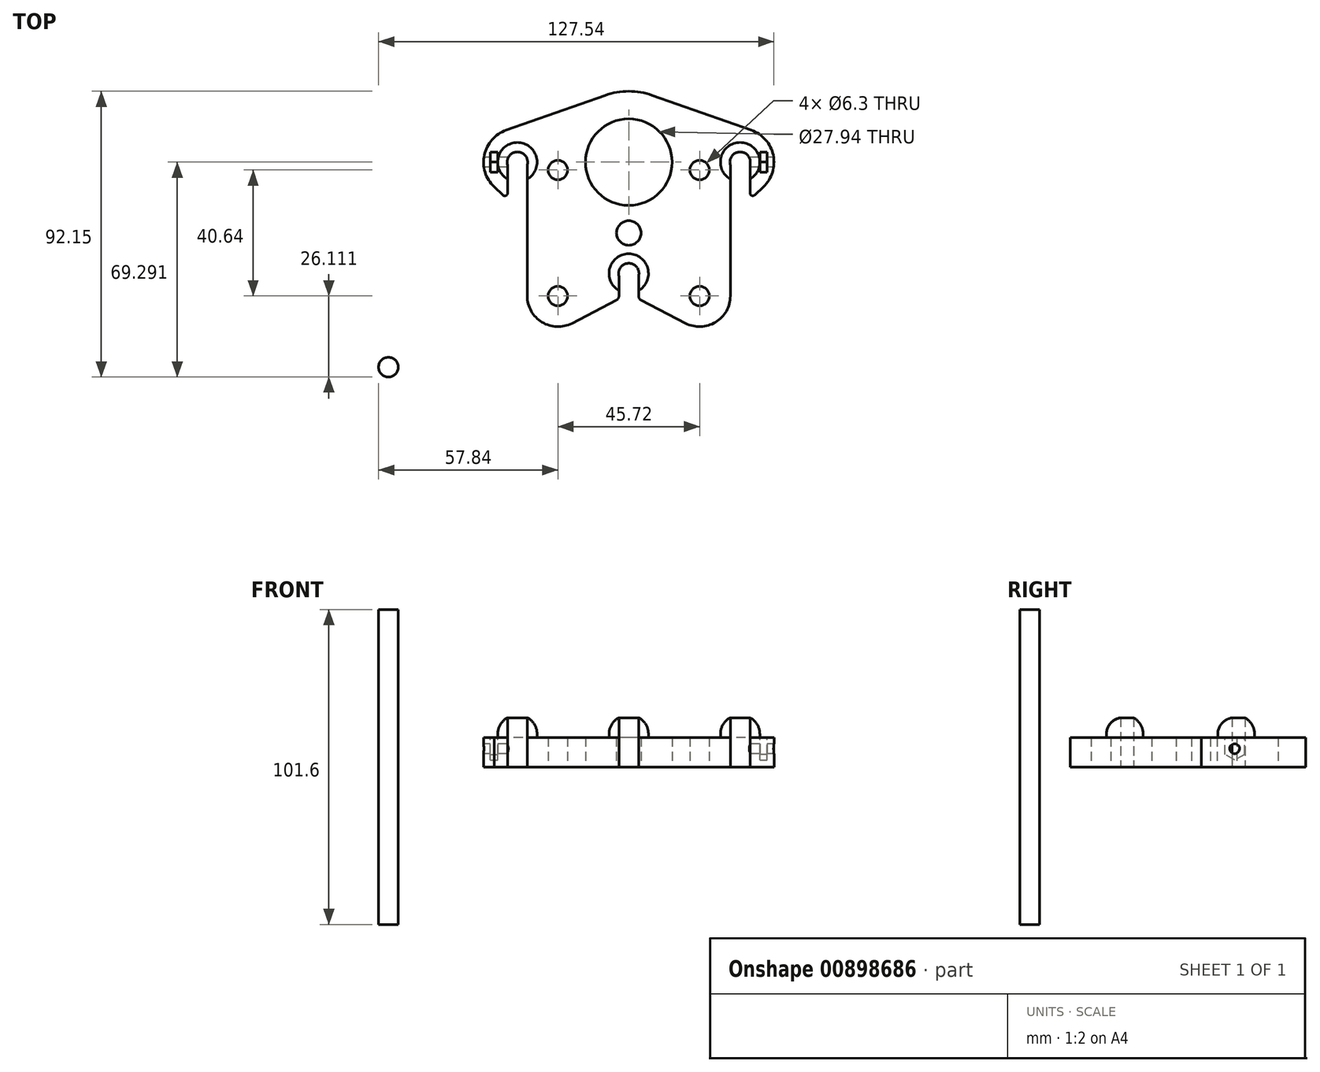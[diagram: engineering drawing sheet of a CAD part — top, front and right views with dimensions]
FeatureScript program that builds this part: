
annotation { "Feature Type Name" : "Feature", "Feature Type Description" : "" }
export const myFeature = defineFeature(function(context is Context, id is Id, definition is map)
    precondition{}
    {
        {
            var Q0;
            Q0=qCreatedBy(makeId("Top.planeOp"),FACE);
            var sketch = newSketch(context, id + "F0", { "sketchPlane" : qUnion([Q0])});
            skArc(sketch, "E0", {"start": v(3.18, -0.9) * mm, "mid": v(0, 3.3) * mm, "end": v(-3.18, -0.9) * mm});
            skArc(sketch, "E1", {"start": v(-32.75, 35.01) * mm, "mid": v(-35.92, 39.22) * mm, "end": v(-39.1, 35.01) * mm});
            skArc(sketch, "E2", {"start": v(39.1, 35.01) * mm, "mid": v(35.92, 39.22) * mm, "end": v(32.75, 35.01) * mm});
            skCircle(sketch, "E3", {"center": v(0, 35.92) * mm, "radius": 16.51 * mm});
            skArc(sketch, "E4.0", {"start": v(-39.55, 46.22) * mm, "mid": v(-46.6, 38.2) * mm, "end": v(-43.45, 28) * mm});
            skArc(sketch, "E5.0", {"start": v(7.6, 57.48) * mm, "mid": v(0, 58.78) * mm, "end": v(-7.6, 57.48) * mm});
            skArc(sketch, "E6.0", {"start": v(43.45, 28) * mm, "mid": v(46.6, 38.2) * mm, "end": v(39.55, 46.22) * mm});
            skLineSegment(sketch, "E7", {"start": v(-39.55, 46.22) * mm, "end": v(-7.6, 57.48) * mm});
            skLineSegment(sketch, "E8", {"start": v(7.6, 57.48) * mm, "end": v(39.55, 46.22) * mm});
            skLineSegment(sketch, "E9", {"start": v(43.45, 28) * mm, "end": v(40.64, 25.34) * mm});
            skCircle(sketch, "E10", {"center": v(-35.92, 35.92) * mm, "radius": 3.18 * mm, "construction": true});
            skCircle(sketch, "E11", {"center": v(35.92, 35.92) * mm, "radius": 3.18 * mm, "construction": true});
            skCircle(sketch, "E12", {"center": v(0, 0) * mm, "radius": 3.18 * mm, "construction": true});
            skLineSegment(sketch, "E13", {"start": v(-39.1, 35.92) * mm, "end": v(-39.1, 25.94) * mm});
            skLineSegment(sketch, "E14", {"start": v(-3.18, 0) * mm, "end": v(-3.17, -7.26) * mm});
            skLineSegment(sketch, "E15", {"start": v(3.17, 0) * mm, "end": v(3.18, -7.26) * mm});
            skPoint(sketch, "E16", {"position": v(-3.18, -0.9) * mm});
            skPoint(sketch, "E17", {"position": v(3.18, -0.9) * mm});
            skLineSegment(sketch, "E18.trimOffspring", {"start": v(-40.65, 25.28) * mm, "end": v(-43.45, 28) * mm});
            skPoint(sketch, "E19.visualSharp", {"position": v(-39.1, 23.76) * mm});
            skArc(sketch, "E19.filletArc", {"start": v(-40.65, 25.28) * mm, "mid": v(-39.66, 25.1) * mm, "end": v(-39.1, 25.94) * mm});
            skLineSegment(sketch, "E20", {"start": v(32.75, 35.92) * mm, "end": v(32.75, -7.26) * mm});
            skLineSegment(sketch, "E21", {"start": v(39.1, 35.92) * mm, "end": v(39.1, 26) * mm});
            skPoint(sketch, "E22.visualSharp", {"position": v(39.1, 23.87) * mm});
            skCircle(sketch, "E23.0", {"center": v(0, 35.92) * mm, "radius": 13.97 * mm});
            skLineSegment(sketch, "E24", {"start": v(0, 35.92) * mm, "end": v(0, 52.43) * mm, "construction": true});
            skArc(sketch, "E25.filletArc", {"start": v(39.1, 26) * mm, "mid": v(39.65, 25.16) * mm, "end": v(40.64, 25.34) * mm});
            skLineSegment(sketch, "E26", {"start": v(-35.92, 35.92) * mm, "end": v(35.92, 35.92) * mm, "construction": true});
            skCircle(sketch, "E27", {"center": v(-22.86, 33.38) * mm, "radius": 3.15 * mm});
            skCircle(sketch, "E28", {"center": v(22.86, 33.38) * mm, "radius": 3.15 * mm});
            skCircle(sketch, "E29", {"center": v(-22.86, -7.26) * mm, "radius": 3.15 * mm});
            skCircle(sketch, "E30", {"center": v(22.86, -7.26) * mm, "radius": 3.15 * mm});
            skLineSegment(sketch, "E31.bottom", {"start": v(-22.86, 33.38) * mm, "end": v(22.86, 33.38) * mm, "construction": true});
            skLineSegment(sketch, "E31.top", {"start": v(-22.86, -7.26) * mm, "end": v(22.86, -7.26) * mm, "construction": true});
            skLineSegment(sketch, "E31.left", {"start": v(-22.86, 33.38) * mm, "end": v(-22.86, -7.26) * mm, "construction": true});
            skLineSegment(sketch, "E31.right", {"start": v(22.86, 33.38) * mm, "end": v(22.86, -7.26) * mm, "construction": true});
            skLineSegment(sketch, "E32", {"start": v(0, 35.92) * mm, "end": v(0, -7.26) * mm, "construction": true});
            skArc(sketch, "E33.0", {"start": v(-32.75, -7.26) * mm, "mid": v(-28, -15.7) * mm, "end": v(-18.3, -16.03) * mm});
            skArc(sketch, "E34.0", {"start": v(18.3, -16.03) * mm, "mid": v(28, -15.7) * mm, "end": v(32.75, -7.26) * mm});
            skLineSegment(sketch, "E35", {"start": v(-4, -8.61) * mm, "end": v(-18.3, -16.03) * mm});
            skLineSegment(sketch, "E36", {"start": v(4, -8.61) * mm, "end": v(18.3, -16.03) * mm});
            skLineSegment(sketch, "E37", {"start": v(-32.75, 35.92) * mm, "end": v(-32.75, -7.26) * mm});
            skPoint(sketch, "E38.visualSharp", {"position": v(-3.17, -8.19) * mm});
            skArc(sketch, "E38.filletArc", {"start": v(-4, -8.61) * mm, "mid": v(-3.4, -8.05) * mm, "end": v(-3.18, -7.26) * mm});
            skPoint(sketch, "E39.visualSharp", {"position": v(3.17, -8.19) * mm});
            skArc(sketch, "E39.filletArc", {"start": v(3.17, -7.26) * mm, "mid": v(3.4, -8.05) * mm, "end": v(4, -8.61) * mm});
            skCircle(sketch, "E40", {"center": v(0, 13.06) * mm, "radius": 3.96 * mm});
            skSolve(sketch);
        }
        {
            var Q0;
            {var subQ5=sQuery(id+"F0.wireOp",EDGE,"E0");Q0=makeQuery(id+"F0.imprint","IMPRINT",FACE,{"disambiguationData":[TD([[makeQuery(id+"F0.imprint","IMPRINT",EDGE,{"derivedFrom":subQ5}),-1.0]])]});}
            extrude(context, id + "F1", {"entities" : qUnion([Q0]), "depth" : 9.52 * mm, "offsetDistance" : 25.4 * mm});
        }
        {
            var Q0;
            Q0=makeQuery(id+"F0.imprint","IMPRINT",FACE,{"disambiguationData":[TD([[makeQuery(id+"F0.imprint","IMPRINT",EDGE,{"derivedFrom":sQuery(id+"F0.wireOp",EDGE,"E3")}),1.0]])]});
            var Q1;
            Q1=makeQuery(id+"F1.opExtrude","CAP_FACE",FACE,{"disambiguationData":[OSD([sQuery(id+"F0.wireOp",EDGE,"E0"),sQuery(id+"F0.wireOp",EDGE,"E1"),sQuery(id+"F0.wireOp",EDGE,"E2"),sQuery(id+"F0.wireOp",EDGE,"E3"),sQuery(id+"F0.wireOp",EDGE,"E4.0"),sQuery(id+"F0.wireOp",EDGE,"E5.0"),sQuery(id+"F0.wireOp",EDGE,"E6.0"),sQuery(id+"F0.wireOp",EDGE,"E7"),sQuery(id+"F0.wireOp",EDGE,"E8"),sQuery(id+"F0.wireOp",EDGE,"E9"),sQuery(id+"F0.wireOp",EDGE,"E13"),sQuery(id+"F0.wireOp",EDGE,"E14"),sQuery(id+"F0.wireOp",EDGE,"E15"),sQuery(id+"F0.wireOp",EDGE,"E18.trimOffspring"),sQuery(id+"F0.wireOp",EDGE,"E19.filletArc"),sQuery(id+"F0.wireOp",EDGE,"E20"),sQuery(id+"F0.wireOp",EDGE,"E21"),sQuery(id+"F0.wireOp",EDGE,"E25.filletArc"),sQuery(id+"F0.wireOp",EDGE,"E27"),sQuery(id+"F0.wireOp",EDGE,"E28"),sQuery(id+"F0.wireOp",EDGE,"E29"),sQuery(id+"F0.wireOp",EDGE,"E30"),sQuery(id+"F0.wireOp",EDGE,"E33.0"),sQuery(id+"F0.wireOp",EDGE,"E34.0"),sQuery(id+"F0.wireOp",EDGE,"E35"),sQuery(id+"F0.wireOp",EDGE,"E36"),sQuery(id+"F0.wireOp",EDGE,"E37"),sQuery(id+"F0.wireOp",EDGE,"E38.filletArc"),sQuery(id+"F0.wireOp",EDGE,"E39.filletArc")])],"isStart":false});
            extrude(context, id + "F2", {"entities" : qUnion([Q0]), "operationType" : NewBodyOperationType.ADD, "endBound" : BoundingType.UP_TO_SURFACE, "depth" : 2.54 * mm, "endBoundEntityFace" : qUnion([Q1]), "offsetDistance" : 6.35 * mm});
        }
        {
            var Q0;
            Q0=makeQuery(id+"F1.opExtrude","CAP_FACE",FACE,{"disambiguationData":[OSD([sQuery(id+"F0.wireOp",EDGE,"E0"),sQuery(id+"F0.wireOp",EDGE,"E1"),sQuery(id+"F0.wireOp",EDGE,"E2"),sQuery(id+"F0.wireOp",EDGE,"E3"),sQuery(id+"F0.wireOp",EDGE,"E4.0"),sQuery(id+"F0.wireOp",EDGE,"E5.0"),sQuery(id+"F0.wireOp",EDGE,"E6.0"),sQuery(id+"F0.wireOp",EDGE,"02fbeba7-076e-4ed0-9f02-67362b93dccf.0"),sQuery(id+"F0.wireOp",EDGE,"E7"),sQuery(id+"F0.wireOp",EDGE,"E8"),sQuery(id+"F0.wireOp",EDGE,"E9"),sQuery(id+"F0.wireOp",EDGE,"bXI39tXD-kIKO-QA8d-uo1d-AjNWw4kzWSzn"),sQuery(id+"F0.wireOp",EDGE,"yvXXFvSa-JQHm-aZvy-wO3q-0ffgoC5Wr51Q"),sQuery(id+"F0.wireOp",EDGE,"E13"),sQuery(id+"F0.wireOp",EDGE,"E14"),sQuery(id+"F0.wireOp",EDGE,"E15"),sQuery(id+"F0.wireOp",EDGE,"1b80de2d-6fcf-4166-8bd7-bc7520118ab3.trimOffspring"),sQuery(id+"F0.wireOp",EDGE,"E18.trimOffspring"),sQuery(id+"F0.wireOp",EDGE,"E19.filletArc"),sQuery(id+"F0.wireOp",EDGE,"30e6a12d-ff62-4460-809b-2951cf116d4f.filletArc"),sQuery(id+"F0.wireOp",EDGE,"3d167f00-72a4-4ff5-8a6d-0d591a0e7773.filletArc"),sQuery(id+"F0.wireOp",EDGE,"E20"),sQuery(id+"F0.wireOp",EDGE,"E21"),sQuery(id+"F0.wireOp",EDGE,"02ed80ea-b338-46f1-988c-5186e078d909.trimOffspring"),sQuery(id+"F0.wireOp",EDGE,"3LgmcLzA-5pnU-fFz7-q1u9-bpeBtAsCO3An"),sQuery(id+"F0.wireOp",EDGE,"4eo9xTR6-c1Fu-en91-zOid-S4E7wj55DmDX"),sQuery(id+"F0.wireOp",EDGE,"E25.filletArc"),sQuery(id+"F0.wireOp",EDGE,"0de4be46-af92-408f-a28e-b5eb566cc358.filletArc"),sQuery(id+"F0.wireOp",EDGE,"cd97e584-8722-4711-bad1-4d169eb79cda.filletArc"),sQuery(id+"F0.wireOp",EDGE,"a80f9f6f-3806-41d0-9fd0-596e0330244b.filletArc"),sQuery(id+"F0.wireOp",EDGE,"743a1c7c-530f-41f0-bede-06812bb20fe3.filletArc")])],"isStart":false});
            var sketch = newSketch(context, id + "F3", { "sketchPlane" : qUnion([Q0])});
            skCircle(sketch, "E41", {"center": v(-35.92, 35.92) * mm, "radius": 6.35 * mm});
            skCircle(sketch, "E42", {"center": v(35.92, 35.92) * mm, "radius": 6.35 * mm});
            skCircle(sketch, "E43", {"center": v(0, 0) * mm, "radius": 6.35 * mm});
            skSolve(sketch);
        }
        {
            var Q0;
            Q0=makeQuery(id+"F1.opExtrude","CAP_FACE",FACE,{"disambiguationData":[OSD([sQuery(id+"F0.wireOp",EDGE,"E0"),sQuery(id+"F0.wireOp",EDGE,"E1"),sQuery(id+"F0.wireOp",EDGE,"E2"),sQuery(id+"F0.wireOp",EDGE,"E3"),sQuery(id+"F0.wireOp",EDGE,"E4.0"),sQuery(id+"F0.wireOp",EDGE,"E5.0"),sQuery(id+"F0.wireOp",EDGE,"E6.0"),sQuery(id+"F0.wireOp",EDGE,"02fbeba7-076e-4ed0-9f02-67362b93dccf.0"),sQuery(id+"F0.wireOp",EDGE,"E7"),sQuery(id+"F0.wireOp",EDGE,"E8"),sQuery(id+"F0.wireOp",EDGE,"E9"),sQuery(id+"F0.wireOp",EDGE,"bXI39tXD-kIKO-QA8d-uo1d-AjNWw4kzWSzn"),sQuery(id+"F0.wireOp",EDGE,"yvXXFvSa-JQHm-aZvy-wO3q-0ffgoC5Wr51Q"),sQuery(id+"F0.wireOp",EDGE,"E13"),sQuery(id+"F0.wireOp",EDGE,"E14"),sQuery(id+"F0.wireOp",EDGE,"E15"),sQuery(id+"F0.wireOp",EDGE,"1b80de2d-6fcf-4166-8bd7-bc7520118ab3.trimOffspring"),sQuery(id+"F0.wireOp",EDGE,"E18.trimOffspring"),sQuery(id+"F0.wireOp",EDGE,"E19.filletArc"),sQuery(id+"F0.wireOp",EDGE,"2f08ad09-a47d-42bd-8f0e-b7f58f6490e4.filletArc"),sQuery(id+"F0.wireOp",EDGE,"30e6a12d-ff62-4460-809b-2951cf116d4f.filletArc"),sQuery(id+"F0.wireOp",EDGE,"3d167f00-72a4-4ff5-8a6d-0d591a0e7773.filletArc"),sQuery(id+"F0.wireOp",EDGE,"E20"),sQuery(id+"F0.wireOp",EDGE,"E21"),sQuery(id+"F0.wireOp",EDGE,"02ed80ea-b338-46f1-988c-5186e078d909.trimOffspring"),sQuery(id+"F0.wireOp",EDGE,"bfc3d6b4-ed7b-404a-8939-94d15189dd00.filletArc"),sQuery(id+"F0.wireOp",EDGE,"E22.filletArc")])],"isStart":false});
            var sketch = newSketch(context, id + "F4", { "sketchPlane" : qUnion([Q0])});
            skPoint(sketch, "E44.center", {"position": v(0, 35.92) * mm});
            skCircle(sketch, "E45", {"center": v(-35.92, 35.92) * mm, "radius": 6.35 * mm});
            skCircle(sketch, "E46", {"center": v(35.92, 35.92) * mm, "radius": 6.35 * mm});
            skCircle(sketch, "E47", {"center": v(0, 0) * mm, "radius": 6.35 * mm});
            skLineSegment(sketch, "E48", {"start": v(-42.27, 39.15) * mm, "end": v(-42.27, 32.7) * mm});
            skLineSegment(sketch, "E49", {"start": v(-42.27, 32.7) * mm, "end": v(-44.6, 32.7) * mm});
            skLineSegment(sketch, "E50", {"start": v(-44.6, 32.7) * mm, "end": v(-44.6, 39.15) * mm});
            skLineSegment(sketch, "E51", {"start": v(-44.6, 39.15) * mm, "end": v(-42.27, 39.15) * mm});
            skLineSegment(sketch, "E52", {"start": v(-35.92, 35.92) * mm, "end": v(-42.27, 35.92) * mm, "construction": true});
            skLineSegment(sketch, "E53", {"start": v(42.27, 32.7) * mm, "end": v(42.27, 39.15) * mm});
            skLineSegment(sketch, "E54", {"start": v(42.27, 39.15) * mm, "end": v(44.6, 39.15) * mm});
            skLineSegment(sketch, "E55", {"start": v(44.6, 39.15) * mm, "end": v(44.6, 32.7) * mm});
            skLineSegment(sketch, "E56", {"start": v(44.6, 32.7) * mm, "end": v(42.27, 32.7) * mm});
            skLineSegment(sketch, "E57", {"start": v(35.92, 35.92) * mm, "end": v(42.27, 35.92) * mm, "construction": true});
            skSolve(sketch);
        }
        {
            var Q0;
            Q0=makeQuery(id+"F4.imprint","IMPRINT",FACE,{"disambiguationData":[TD([[makeQuery(id+"F4.imprint","IMPRINT",EDGE,{"derivedFrom":sQuery(id+"F4.wireOp",EDGE,"E44.2.0")}),-1.0]])]});
            var Q1;
            {var subQ3=sQuery(id+"F4.wireOp",EDGE,"d1FFw4VD-CotE-ErUC-aBlM-ySrozfUtPZIG");Q1=makeQuery(id+"F4.imprint","IMPRINT",FACE,{"disambiguationData":[TD([[makeQuery(id+"F4.imprint","IMPRINT",EDGE,{"derivedFrom":subQ3}),-1.0]])]});}
            var Q2;
            Q2=makeQuery(id+"F4.imprint","IMPRINT",FACE,{"disambiguationData":[TD([[makeQuery(id+"F4.imprint","IMPRINT",EDGE,{"derivedFrom":sQuery(id+"F4.wireOp",EDGE,"E44.1.0")}),-1.0]])]});
            var Q3;
            {var subQ0=sQuery(id+"F4.wireOp",EDGE,"E49");Q3=makeQuery(id+"F4.imprint","IMPRINT",FACE,{"disambiguationData":[TD([[makeQuery(id+"F4.imprint","IMPRINT",EDGE,{"derivedFrom":subQ0}),-1.0]])]});}
            var Q4;
            {var subQ0=sQuery(id+"F4.wireOp",EDGE,"E54");Q4=makeQuery(id+"F4.imprint","IMPRINT",FACE,{"disambiguationData":[TD([[makeQuery(id+"F4.imprint","IMPRINT",EDGE,{"derivedFrom":subQ0}),-1.0]])]});}
            var Q5;
            Q5=makeQuery(id+"F4.imprint","IMPRINT",FACE,{"disambiguationData":[TD([[makeQuery(id+"F4.imprint","IMPRINT",EDGE,{"derivedFrom":sQuery(id+"F4.wireOp",EDGE,"1bb13d12-811f-4404-9e1d-75ced0edb1cc")}),-1.0]])]});
            extrude(context, id + "F5", {"entities" : qUnion([Q0, Q1, Q2, Q3, Q4, Q5]), "operationType" : NewBodyOperationType.REMOVE, "oppositeDirection" : true, "depth" : 8.64 * mm, "offsetDistance" : 25.4 * mm});
        }
        {
            var Q0;
            Q0=makeQuery(id+"F5.boolean.opBoolean","COPY",EDGE,{"derivedFrom":makeQuery(id+"F5.opExtrude","CAP_EDGE",EDGE,{"disambiguationData":[OSD([sQuery(id+"F4.wireOp",EDGE,"E44.1.1")])],"isStart":false})});
            var Q1;
            Q1=makeQuery(id+"F5.boolean.opBoolean","COPY",EDGE,{"derivedFrom":makeQuery(id+"F5.opExtrude","CAP_EDGE",EDGE,{"disambiguationData":[OSD([sQuery(id+"F4.wireOp",EDGE,"E44.1.3")])],"isStart":false})});
            var Q2;
            Q2=makeQuery(id+"F5.boolean.opBoolean","COPY",EDGE,{"derivedFrom":makeQuery(id+"F5.opExtrude","CAP_EDGE",EDGE,{"disambiguationData":[OSD([sQuery(id+"F4.wireOp",EDGE,"d1FFw4VD-CotE-ErUC-aBlM-ySrozfUtPZIG")])],"isStart":false})});
            var Q3;
            Q3=makeQuery(id+"F5.boolean.opBoolean","COPY",EDGE,{"derivedFrom":makeQuery(id+"F5.opExtrude","CAP_EDGE",EDGE,{"disambiguationData":[OSD([sQuery(id+"F4.wireOp",EDGE,"UtWCcdUI-wfrM-d3JI-pGr6-eE53RfRw4Zsa")])],"isStart":false})});
            var Q4;
            Q4=makeQuery(id+"F5.boolean.opBoolean","COPY",EDGE,{"derivedFrom":makeQuery(id+"F5.opExtrude","CAP_EDGE",EDGE,{"disambiguationData":[OSD([sQuery(id+"F4.wireOp",EDGE,"E44.2.3")])],"isStart":false})});
            var Q5;
            Q5=makeQuery(id+"F5.boolean.opBoolean","COPY",EDGE,{"derivedFrom":makeQuery(id+"F5.opExtrude","CAP_EDGE",EDGE,{"disambiguationData":[OSD([sQuery(id+"F4.wireOp",EDGE,"E44.2.1")])],"isStart":false})});
            var Q6;
            Q6=makeQuery(id+"F5.boolean.opBoolean","COPY",EDGE,{"derivedFrom":makeQuery(id+"F5.opExtrude","CAP_EDGE",EDGE,{"disambiguationData":[OSD([sQuery(id+"F4.wireOp",EDGE,"E51")])],"isStart":false})});
            var Q7;
            Q7=makeQuery(id+"F5.boolean.opBoolean","COPY",EDGE,{"derivedFrom":makeQuery(id+"F5.opExtrude","CAP_EDGE",EDGE,{"disambiguationData":[OSD([sQuery(id+"F4.wireOp",EDGE,"E49")])],"isStart":false})});
            var Q8;
            Q8=makeQuery(id+"F5.boolean.opBoolean","COPY",EDGE,{"derivedFrom":makeQuery(id+"F5.opExtrude","CAP_EDGE",EDGE,{"disambiguationData":[OSD([sQuery(id+"F4.wireOp",EDGE,"236dffc3-8eaa-4971-9524-ae12a32c2ead")])],"isStart":false})});
            var Q9;
            Q9=makeQuery(id+"F5.boolean.opBoolean","COPY",EDGE,{"derivedFrom":makeQuery(id+"F5.opExtrude","CAP_EDGE",EDGE,{"disambiguationData":[OSD([sQuery(id+"F4.wireOp",EDGE,"c035f3bf-e4a5-496b-bfbc-999cd9edc6f8")])],"isStart":false})});
            var Q10;
            Q10=makeQuery(id+"F5.boolean.opBoolean","COPY",EDGE,{"derivedFrom":makeQuery(id+"F5.opExtrude","CAP_EDGE",EDGE,{"disambiguationData":[OSD([sQuery(id+"F4.wireOp",EDGE,"E54")])],"isStart":false})});
            var Q11;
            Q11=makeQuery(id+"F5.boolean.opBoolean","COPY",EDGE,{"derivedFrom":makeQuery(id+"F5.opExtrude","CAP_EDGE",EDGE,{"disambiguationData":[OSD([sQuery(id+"F4.wireOp",EDGE,"E56")])],"isStart":false})});
            chamfer(context, id + "F6", {"entities" : qUnion([Q0, Q1, Q2, Q3, Q4, Q5, Q6, Q7, Q8, Q9, Q10, Q11]), "chamferType" : ChamferType.OFFSET_ANGLE, "width" : 3.17 * mm, "oppositeDirection" : false, "angle" : 60 * degree, "tangentPropagation" : true});
        }
        {
            var Q0;
            {var subQ5=makeQuery(id+"F1.opExtrude","CAP_EDGE",EDGE,{"disambiguationData":[OSD([sQuery(id+"F0.wireOp",EDGE,"E1")])],"isStart":false});Q0=makeQuery(id+"F3.imprint","IMPRINT",FACE,{"disambiguationData":[TD([[makeQuery(id+"F3.imprint","IMPRINT",EDGE,{"derivedFrom":subQ5}),-1.0]])]});}
            var Q1;
            {var subQ5=makeQuery(id+"F1.opExtrude","CAP_EDGE",EDGE,{"disambiguationData":[OSD([sQuery(id+"F0.wireOp",EDGE,"E2")])],"isStart":false});Q1=makeQuery(id+"F3.imprint","IMPRINT",FACE,{"disambiguationData":[TD([[makeQuery(id+"F3.imprint","IMPRINT",EDGE,{"derivedFrom":subQ5}),-1.0]])]});}
            var Q2;
            {var subQ5=makeQuery(id+"F1.opExtrude","CAP_EDGE",EDGE,{"disambiguationData":[OSD([sQuery(id+"F0.wireOp",EDGE,"E0")])],"isStart":false});Q2=makeQuery(id+"F3.imprint","IMPRINT",FACE,{"disambiguationData":[TD([[makeQuery(id+"F3.imprint","IMPRINT",EDGE,{"derivedFrom":subQ5}),-1.0]])]});}
            extrude(context, id + "F7", {"entities" : qUnion([Q0, Q1, Q2]), "operationType" : NewBodyOperationType.ADD, "depth" : 6.35 * mm, "offsetDistance" : 25.4 * mm});
        }
        {
            var Q0;
            Q0=makeQuery(id+"F7.opExtrude","CAP_EDGE",EDGE,{"disambiguationData":[OSD([sQuery(id+"F3.wireOp",EDGE,"E41")])],"isStart":false});
            var Q1;
            Q1=makeQuery(id+"F7.opExtrude","CAP_EDGE",EDGE,{"disambiguationData":[OSD([sQuery(id+"F3.wireOp",EDGE,"E42")])],"isStart":false});
            var Q2;
            Q2=makeQuery(id+"F7.opExtrude","CAP_EDGE",EDGE,{"disambiguationData":[OSD([sQuery(id+"F3.wireOp",EDGE,"E43")])],"isStart":false});
            fillet(context, id + "F8", {"entities" : qUnion([Q0, Q1, Q2]), "radius" : 6.1 * mm, "tangentPropagation" : true, "allowEdgeOverflow" : false});
        }
        {
            var Q0;
            Q0=makeQuery(id+"F5.boolean.opBoolean","COPY",FACE,{"derivedFrom":makeQuery(id+"F5.opExtrude","SWEPT_FACE",FACE,{"disambiguationData":[OSD([sQuery(id+"F4.wireOp",EDGE,"E50")])]})});
            var sketch = newSketch(context, id + "F9", { "sketchPlane" : qUnion([Q0])});
            skLineSegment(sketch, "E58", {"start": v(39.03, 4.06) * mm, "end": v(35.86, 2.24) * mm});
            skLineSegment(sketch, "E59", {"start": v(35.86, 2.24) * mm, "end": v(32.7, 4.06) * mm});
            skLineSegment(sketch, "E60", {"start": v(32.7, 4.06) * mm, "end": v(32.7, 7.72) * mm});
            skLineSegment(sketch, "E61", {"start": v(39.03, 7.72) * mm, "end": v(39.03, 4.06) * mm});
            skLineSegment(sketch, "E62", {"start": v(39.03, 7.72) * mm, "end": v(35.86, 9.55) * mm});
            skLineSegment(sketch, "E63", {"start": v(35.86, 9.55) * mm, "end": v(32.7, 7.72) * mm});
            skLineSegment(sketch, "E64", {"start": v(35.86, 2.24) * mm, "end": v(35.86, 5.9) * mm, "construction": true});
            skLineSegment(sketch, "E65", {"start": v(35.86, 5.9) * mm, "end": v(32.7, 4.06) * mm, "construction": true});
            skLineSegment(sketch, "E66", {"start": v(35.86, 5.9) * mm, "end": v(39.03, 7.72) * mm, "construction": true});
            skLineSegment(sketch, "E67", {"start": v(35.86, 5.9) * mm, "end": v(35.86, 9.55) * mm, "construction": true});
            skCircle(sketch, "E68", {"center": v(35.86, 5.9) * mm, "radius": 1.59 * mm});
            skSolve(sketch);
        }
        {
            var Q0;
            Q0=makeQuery(id+"F5.boolean.opBoolean","COPY",FACE,{"derivedFrom":makeQuery(id+"F5.opExtrude","SWEPT_FACE",FACE,{"disambiguationData":[OSD([sQuery(id+"F4.wireOp",EDGE,"E55")])]})});
            var sketch = newSketch(context, id + "F10", { "sketchPlane" : qUnion([Q0])});
            skLineSegment(sketch, "E69", {"start": v(-32.7, 4.06) * mm, "end": v(-35.86, 2.24) * mm});
            skLineSegment(sketch, "E70", {"start": v(-35.86, 2.24) * mm, "end": v(-39.03, 4.06) * mm});
            skLineSegment(sketch, "E71", {"start": v(-39.03, 4.06) * mm, "end": v(-39.03, 7.72) * mm});
            skLineSegment(sketch, "E72", {"start": v(-32.7, 7.72) * mm, "end": v(-32.7, 4.06) * mm});
            skLineSegment(sketch, "E73", {"start": v(-32.7, 7.72) * mm, "end": v(-35.86, 9.55) * mm});
            skLineSegment(sketch, "E74", {"start": v(-35.86, 9.55) * mm, "end": v(-39.03, 7.72) * mm});
            skLineSegment(sketch, "E75", {"start": v(-35.86, 2.24) * mm, "end": v(-35.86, 5.9) * mm, "construction": true});
            skLineSegment(sketch, "E76", {"start": v(-35.86, 5.9) * mm, "end": v(-39.03, 4.06) * mm, "construction": true});
            skLineSegment(sketch, "E77", {"start": v(-35.86, 5.9) * mm, "end": v(-32.7, 7.72) * mm, "construction": true});
            skLineSegment(sketch, "E78", {"start": v(-35.86, 5.9) * mm, "end": v(-35.86, 9.55) * mm, "construction": true});
            skCircle(sketch, "E79", {"center": v(-35.86, 5.9) * mm, "radius": 1.59 * mm});
            skSolve(sketch);
        }
        {
            var Q0;
            Q0=makeQuery(id+"F10.imprint","IMPRINT",FACE,{"disambiguationData":[TD([[makeQuery(id+"F10.imprint","IMPRINT",EDGE,{"derivedFrom":sQuery(id+"F10.wireOp",EDGE,"E79")}),1.0]])]});
            var Q1;
            Q1=sQuery(id+"F10.wireOp",EDGE,"E79");
            extrude(context, id + "F11", {"entities" : qUnion([Q0]), "operationType" : NewBodyOperationType.REMOVE, "surfaceEntities" : qUnion([Q1]), "oppositeDirection" : true, "depth" : 12.7 * mm, "offsetDistance" : 25.4 * mm, "symmetric" : true});
        }
        {
            var Q0;
            Q0=makeQuery(id+"F9.imprint","IMPRINT",FACE,{"disambiguationData":[TD([[makeQuery(id+"F9.imprint","IMPRINT",EDGE,{"derivedFrom":sQuery(id+"F9.wireOp",EDGE,"E68")}),1.0]])]});
            extrude(context, id + "F12", {"entities" : qUnion([Q0]), "operationType" : NewBodyOperationType.REMOVE, "depth" : 12.7 * mm, "offsetDistance" : 25.4 * mm, "symmetric" : true});
        }
        {
            var Q0;
            Q0=qCreatedBy(makeId("Top.planeOp"),FACE);
            var sketch = newSketch(context, id + "F13", { "sketchPlane" : qUnion([Q0])});
            skCircle(sketch, "E80", {"center": v(-77.52, -30.2) * mm, "radius": 3.18 * mm});
            skSolve(sketch);
        }
        {
            var Q0;
            Q0=makeQuery(id+"F13.imprint","IMPRINT",FACE,{"disambiguationData":[TD([[makeQuery(id+"F13.imprint","IMPRINT",EDGE,{"derivedFrom":sQuery(id+"F13.wireOp",EDGE,"E80")}),1.0]])]});
            extrude(context, id + "F14", {"entities" : qUnion([Q0]), "depth" : 101.6 * mm, "offsetDistance" : 25.4 * mm, "symmetric" : true});
        }
    });
